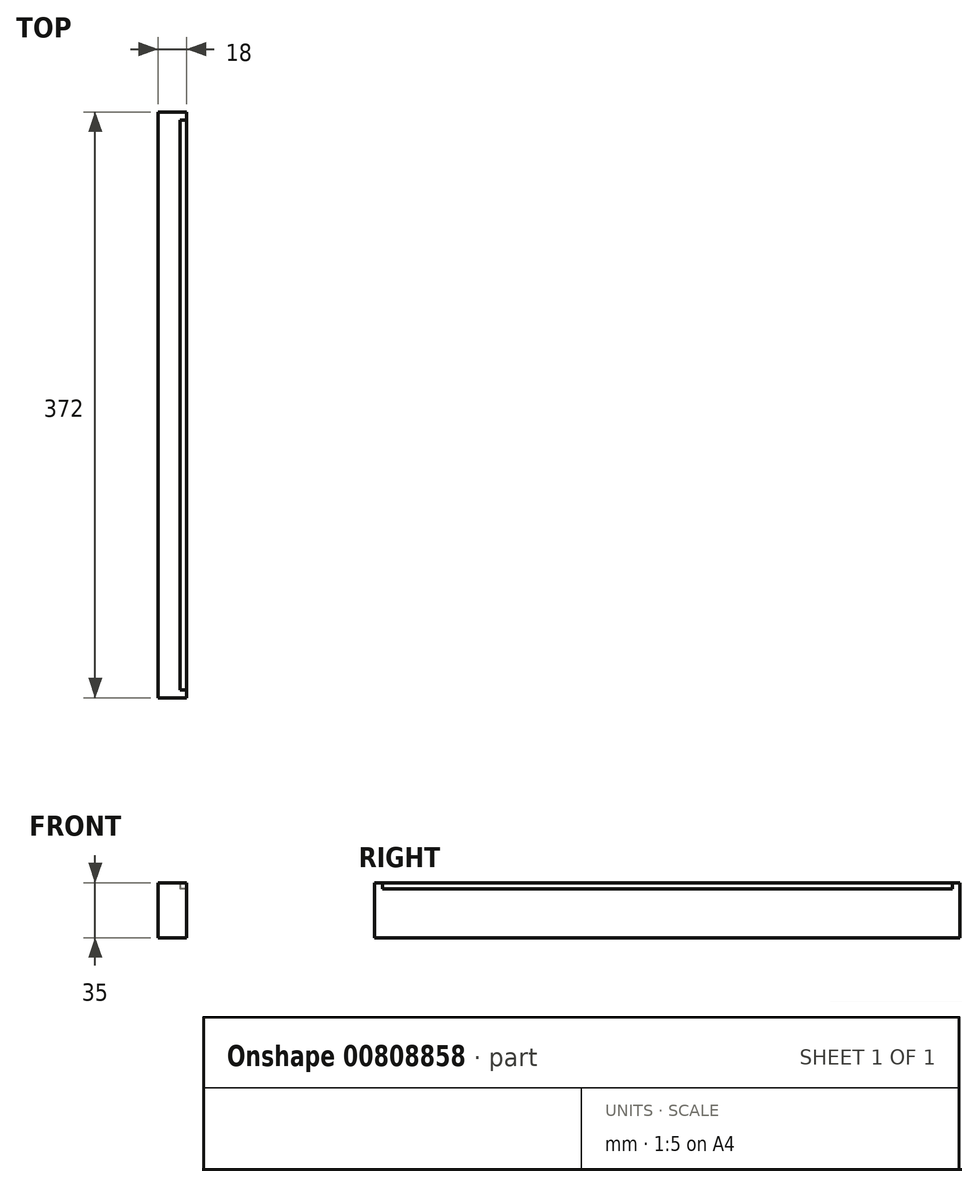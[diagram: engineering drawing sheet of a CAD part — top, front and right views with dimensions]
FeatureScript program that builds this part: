
annotation { "Feature Type Name" : "Feature", "Feature Type Description" : "" }
export const myFeature = defineFeature(function(context is Context, id is Id, definition is map)
    precondition{}
    {
        {
            var Q0;
            Q0=qCreatedBy(makeId("Right.planeOp"),FACE);
            var sketch = newSketch(context, id + "F0", { "sketchPlane" : qUnion([Q0])});
            skLineSegment(sketch, "E0.bottom", {"start": v(0, 0) * mm, "end": v(372, 0) * mm});
            skLineSegment(sketch, "E0.top", {"start": v(0, 35) * mm, "end": v(372, 35) * mm});
            skLineSegment(sketch, "E0.left", {"start": v(0, 0) * mm, "end": v(0, 35) * mm});
            skLineSegment(sketch, "E0.right", {"start": v(372, 0) * mm, "end": v(372, 35) * mm});
            skLineSegment(sketch, "E1.top", {"start": v(0, 31) * mm, "end": v(372, 31) * mm});
            skLineSegment(sketch, "E1.left", {"start": v(0, 35) * mm, "end": v(0, 31) * mm});
            skLineSegment(sketch, "E1.right", {"start": v(372, 35) * mm, "end": v(372, 31) * mm});
            skLineSegment(sketch, "E2.bottom", {"start": v(0, 35) * mm, "end": v(5, 35) * mm});
            skLineSegment(sketch, "E2.top", {"start": v(0, 31) * mm, "end": v(5, 31) * mm});
            skLineSegment(sketch, "E2.right", {"start": v(5, 35) * mm, "end": v(5, 31) * mm});
            skLineSegment(sketch, "E3.bottom", {"start": v(372, 35) * mm, "end": v(367, 35) * mm});
            skLineSegment(sketch, "E3.top", {"start": v(372, 31) * mm, "end": v(367, 31) * mm});
            skLineSegment(sketch, "E3.right", {"start": v(367, 35) * mm, "end": v(367, 31) * mm});
            skSolve(sketch);
        }
        {
            var Q0;
            {var subQ4=sQuery(id+"F0.wireOp",EDGE,"E0.bottom");Q0=makeQuery(id+"F0.imprint","IMPRINT",FACE,{"disambiguationData":[TD([[makeQuery(id+"F0.imprint","IMPRINT",EDGE,{"derivedFrom":subQ4}),1.0]])]});}
            var Q1;
            {var subQ0=sQuery(id+"F0.wireOp",EDGE,"E2.right");Q1=makeQuery(id+"F0.imprint","IMPRINT",FACE,{"disambiguationData":[TD([[makeQuery(id+"F0.imprint","IMPRINT",EDGE,{"derivedFrom":subQ0}),-1.0]])]});}
            var Q2;
            {var subQ3=sQuery(id+"F0.wireOp",EDGE,"E3.right");Q2=makeQuery(id+"F0.imprint","IMPRINT",FACE,{"disambiguationData":[TD([[makeQuery(id+"F0.imprint","IMPRINT",EDGE,{"derivedFrom":subQ3}),1.0]])]});}
            extrude(context, id + "F1", {"entities" : qUnion([Q0, Q1, Q2]), "depth" : 18 * mm, "offsetDistance" : 25 * mm});
        }
        {
            var Q0;
            {var subQ0=sQuery(id+"F0.wireOp",EDGE,"E2.right");Q0=makeQuery(id+"F0.imprint","IMPRINT",FACE,{"disambiguationData":[TD([[makeQuery(id+"F0.imprint","IMPRINT",EDGE,{"derivedFrom":subQ0}),1.0]])]});}
            extrude(context, id + "F2", {"entities" : qUnion([Q0]), "operationType" : NewBodyOperationType.ADD, "depth" : 14 * mm, "offsetDistance" : 25 * mm});
        }
    });
